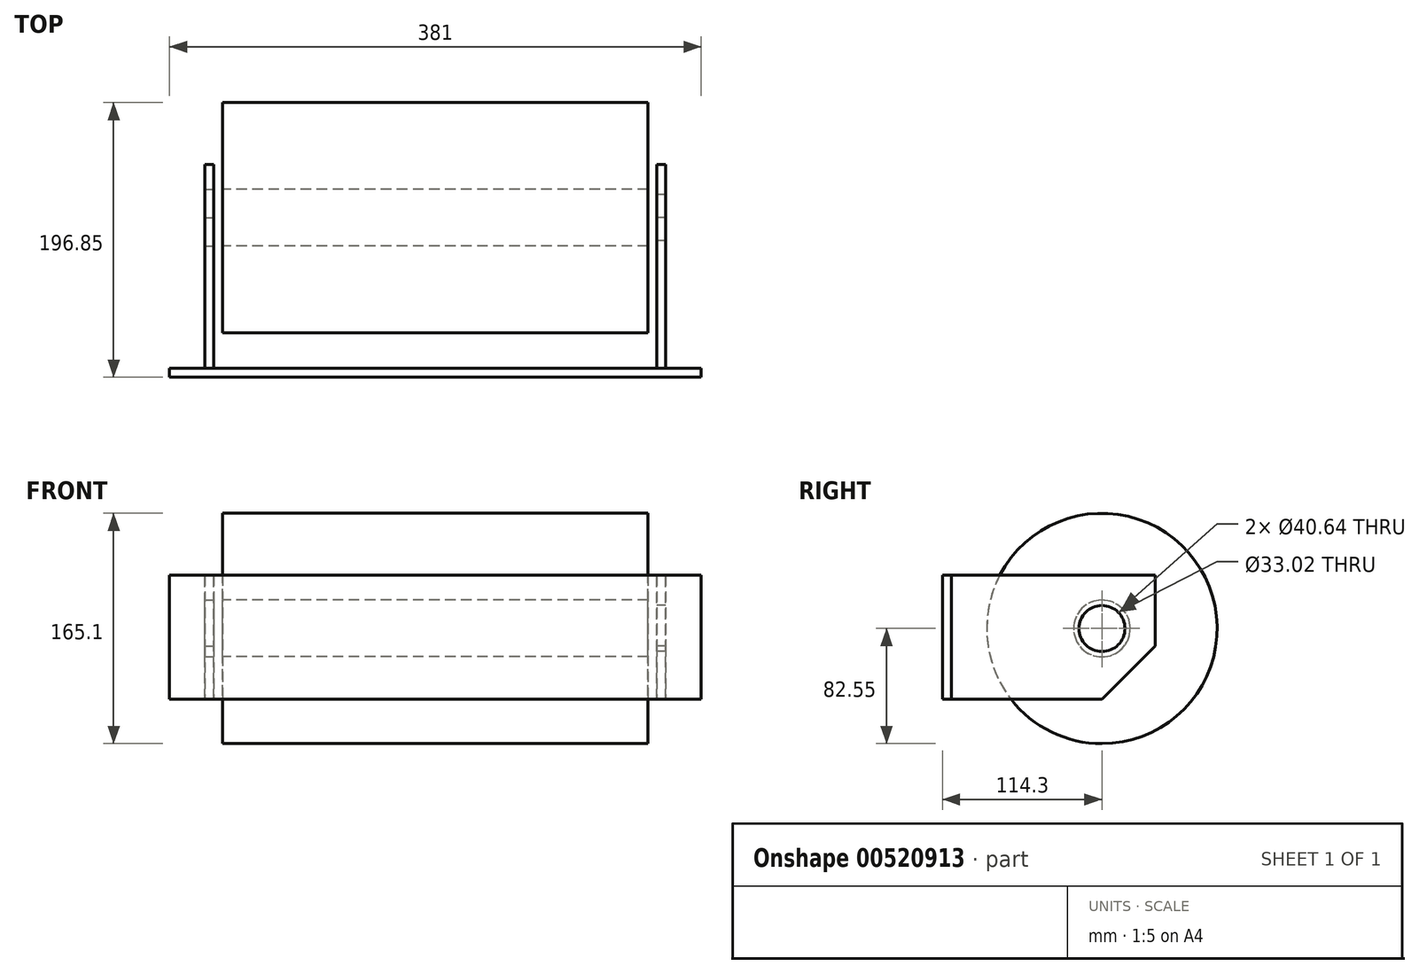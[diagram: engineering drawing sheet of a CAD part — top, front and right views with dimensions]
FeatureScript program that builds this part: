
annotation { "Feature Type Name" : "Feature", "Feature Type Description" : "" }
export const myFeature = defineFeature(function(context is Context, id is Id, definition is map)
    precondition{}
    {
        {
            var Q0;
            Q0=qCreatedBy(makeId("Right.planeOp"),FACE);
            var sketch = newSketch(context, id + "F0", { "sketchPlane" : qUnion([Q0])});
            skCircle(sketch, "E0", {"center": v(0, 0) * mm, "radius": 20.32 * mm});
            skCircle(sketch, "E1", {"center": v(0, 0) * mm, "radius": 82.55 * mm});
            skSolve(sketch);
        }
        {
            var Q0;
            Q0 = qSketchRegion(id + "F0", true);
            extrude(context, id + "F1", {"entities" : qUnion([Q0]), "endBound" : BoundingType.SYMMETRIC, "depth" : 304.8 * mm, "offsetDistance" : 25.4 * mm});
        }
        {
            var Q0;
            Q0=makeQuery(id+"F1.opExtrude","CAP_FACE",FACE,{"disambiguationData":[OSD([sQuery(id+"F0.wireOp",EDGE,"E0"),sQuery(id+"F0.wireOp",EDGE,"E1")])],"isStart":false});
            var sketch = newSketch(context, id + "F2", { "sketchPlane" : qUnion([Q0])});
            skLineSegment(sketch, "E2", {"start": v(-107.95, 38.1) * mm, "end": v(38.1, 38.1) * mm});
            skLineSegment(sketch, "E3", {"start": v(38.1, 38.1) * mm, "end": v(38.1, -12.7) * mm});
            skLineSegment(sketch, "E4", {"start": v(38.1, -12.7) * mm, "end": v(0, -50.8) * mm});
            skLineSegment(sketch, "E5", {"start": v(0, -50.8) * mm, "end": v(-107.95, -50.8) * mm});
            skLineSegment(sketch, "E6", {"start": v(-107.95, -50.8) * mm, "end": v(-107.95, 38.1) * mm});
            skLineSegment(sketch, "E7", {"start": v(38.1, -12.7) * mm, "end": v(38.1, -38.1) * mm, "construction": true});
            skCircle(sketch, "E8.0", {"center": v(0, 0) * mm, "radius": 82.55 * mm, "construction": true});
            skCircle(sketch, "E9", {"center": v(0, 0) * mm, "radius": 16.51 * mm});
            skSolve(sketch);
        }
        {
            var Q0;
            Q0 = qSketchRegion(id + "F2", true);
            extrude(context, id + "F3", {"entities" : qUnion([Q0]), "depth" : 12.7 * mm, "offsetDistance" : 25.4 * mm});
        }
        {
            var Q0;
            Q0=makeQuery(id+"F1.opExtrude","CAP_FACE",FACE,{"disambiguationData":[OSD([sQuery(id+"F0.wireOp",EDGE,"E0"),sQuery(id+"F0.wireOp",EDGE,"E1")])],"isStart":true});
            var sketch = newSketch(context, id + "F4", { "sketchPlane" : qUnion([Q0])});
            skLineSegment(sketch, "E10.0.0", {"start": v(0, -50.8) * mm, "end": v(107.95, -50.8) * mm});
            skLineSegment(sketch, "E10.0.1", {"start": v(107.95, -50.8) * mm, "end": v(107.95, 38.1) * mm});
            skLineSegment(sketch, "E10.0.2", {"start": v(107.95, 38.1) * mm, "end": v(-38.1, 38.1) * mm});
            skLineSegment(sketch, "E10.0.3", {"start": v(-38.1, 38.1) * mm, "end": v(-38.1, -12.7) * mm});
            skLineSegment(sketch, "E10.0.4", {"start": v(-38.1, -12.7) * mm, "end": v(0, -50.8) * mm});
            skCircle(sketch, "E11.0", {"center": v(0, 0) * mm, "radius": 16.51 * mm});
            skSolve(sketch);
        }
        {
            var Q0;
            {var subQ1=sQuery(id+"F4.wireOp",EDGE,"E10.0.3");Q0=makeQuery(id+"F4.imprint","IMPRINT",FACE,{"disambiguationData":[TD([[makeQuery(id+"F4.imprint","IMPRINT",EDGE,{"derivedFrom":subQ1}),1.0]])]});}
            var Q1;
            {var subQ0=sQuery(id+"F4.wireOp",EDGE,"E10.0.1");Q1=makeQuery(id+"F4.imprint","IMPRINT",FACE,{"disambiguationData":[TD([[makeQuery(id+"F4.imprint","IMPRINT",EDGE,{"derivedFrom":subQ0}),1.0]])]});}
            extrude(context, id + "F5", {"entities" : qUnion([Q0, Q1]), "depth" : 12.7 * mm, "offsetDistance" : 25.4 * mm});
        }
        {
            var Q0;
            Q0 = qSketchRegion(id + "F2", true);
            extrude(context, id + "F6", {"entities" : qUnion([Q0]), "operationType" : NewBodyOperationType.REMOVE, "depth" : 6.35 * mm, "offsetDistance" : 25.4 * mm});
        }
        {
            var Q0;
            Q0 = qSketchRegion(id + "F4", true);
            extrude(context, id + "F7", {"entities" : qUnion([Q0]), "operationType" : NewBodyOperationType.REMOVE, "depth" : 6.35 * mm, "offsetDistance" : 25.4 * mm});
        }
        {
            var Q0;
            Q0=makeQuery(id+"F5.opExtrude","SWEPT_FACE",FACE,{"disambiguationData":[OSD([sQuery(id+"F4.wireOp",EDGE,"E10.0.1")])]});
            var sketch = newSketch(context, id + "F8", { "sketchPlane" : qUnion([Q0])});
            skLineSegment(sketch, "E12.0", {"start": v(-190.5, -50.8) * mm, "end": v(-190.5, 38.1) * mm});
            skLineSegment(sketch, "E13.0", {"start": v(190.5, -50.8) * mm, "end": v(190.5, 38.1) * mm});
            skLineSegment(sketch, "E14", {"start": v(-190.5, 38.1) * mm, "end": v(190.5, 38.1) * mm});
            skLineSegment(sketch, "E15", {"start": v(190.5, -50.8) * mm, "end": v(-190.5, -50.8) * mm});
            skSolve(sketch);
        }
        {
            var Q0;
            Q0 = qSketchRegion(id + "F8", true);
            extrude(context, id + "F9", {"entities" : qUnion([Q0]), "depth" : 6.35 * mm, "offsetDistance" : 25.4 * mm});
        }
    });
